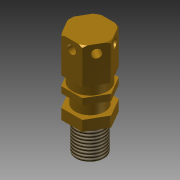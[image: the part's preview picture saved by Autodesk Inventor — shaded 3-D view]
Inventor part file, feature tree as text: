
AUTODESK INVENTOR PART (.ipt)
format: ipt  version: 2014 (Build 180170000, 170)  size: 202,240 bytes
history: native  units: mm (DEFAULTED — no unit token found)
features: sketch x9, projected_geometry x9, extrude x8, pattern_circular x1, thread x1, fillet x1, revolve x1
ambient origin geometry x8: Origin, YZ Plane, XZ Plane, XY Plane, X Axis, Y Axis, Z Axis, Center Point
bodies: Solid1 (feature_tree)
feature tree (30):
  extrude  "Extrusion1"  Depth=17.0mm TaperAngle=0.0deg
  extrude  "Extrusion2"  Depth=4.5mm TaperAngle=0.0deg
  extrude  "Extrusion3"  Depth=14.0mm
  extrude  "Extrusion4"  Depth=5.0mm TaperAngle=0.0deg
  extrude  "Extrusion5"  Depth=14.5mm TaperAngle=0.0deg
  extrude  "Extrusion6"  Depth=47.5mm TaperAngle=0.0deg
  extrude  "Extrusion7"  Depth=4.0mm
  extrude  "Extrusion8"  Depth=30.0mm TaperAngle=360.0deg
  pattern_circular  "Circular Pattern1"  Angle=45.0deg  [1 undecoded]
  thread  "Thread1"  [1 undecoded]
  fillet  "Fillet1"  [1 undecoded]
  revolve  "Revolution2"  [1 undecoded]
  sketch  "Sketch1"  dims[d0=17.5mm d1=17.0mm d2=0.0mm]
  sketch  "Sketch2"  dims[d3=16.5mm d4=4.5mm d5=0.0mm]
  projected_geometry  "Projected Loop1"
  sketch  "Sketch3"  dims[d6=3.0mm d7=0.0mm d8=14.0mm]
  projected_geometry  "Projected Loop2"
  sketch  "Sketch4"  dims[d9=6.0mm d10=0.0mm d11=5.0mm d12=0.0mm]
  projected_geometry  "Projected Loop3"
  sketch  "Sketch5"  dims[d13=13.25mm d14=14.5mm d15=0.0mm]
  projected_geometry  "Projected Loop4"
  sketch  "Sketch6"  dims[d16=5.0mm d17=47.5mm d18=0.0mm]
  projected_geometry  "Projected Loop5"
  sketch  "Sketch7"  dims[d19=4.0mm d20=4.0mm]
  projected_geometry  "Projected Loop6"
  sketch  "Sketch8"  dims[d21=40.25mm d22=0.0mm d23=30.0mm d25=360.0deg]
  projected_geometry  "Projected Loop7"
  sketch  "Sketch10"  dims[d26=10.0mm d27=0.0mm d28=0.5mm d32=45.0deg d33=1.0mm d34=90.0deg]
  projected_geometry  "Projected Loop8"
  projected_geometry  "Projected Loop9"
note: 4 required parameter values undecoded (feature->parameter linkage not recoverable at this tier; creation-order binding heuristic only, values carry confidence <= 0.55)
